# Revit family: FU_Table_Sandler_592-XT
name_source: partatom
category: Furniture
units: mm (PartAtom-declared; Revit-internal decimal feet)

## family parameters
Always vertical = Yes
Cut with Voids When Loaded = No
OmniClass Number = 23.40.20.00
OmniClass Title = General Furniture and Specialties
Room Calculation Point = No
Shared = No
Work Plane-Based = No

## types (5) — shared parameters
Depth = 605 mm  [stored 1.98491 ft]
Description = Table base in stainless steel.
Height = 720 mm  [stored 2.3622 ft]
Manufacturer = Sandler
Model = 592 XT
Top Elevation = 720 mm  [stored 2.3622 ft]
URL = https://www.sandlerseating.com
Width = 605 mm  [stored 1.98491 ft]
zero-valued in all types: Default Elevation

## per-type parameters (varying)
| type | Top Size |
| 592 XT - 40" Square Top (100cm) | FU_TableTops_MT Sqr : 40" Square (100cm) |
| 592 XT - 44" Square Top (110cm) | FU_TableTops_MT Sqr : 44" Square (110cm) |
| 592 XT - 44" Round Top (110cm) | FU_TableTops_MT Rnd : 44" Round (110cm) |
| 592 XT - 51" Round Top (130cm) | FU_TableTops_MT Rnd : 51" Round (130cm) |
| 592 XT - 48" Round Top (120cm) | FU_TableTops_MT Rnd : 47" Round (120cm) |

note: [stored X ft] marks values corroborated as IEEE doubles in the binary element streams (Revit-internal decimal feet)

## geometry (parser evidence)
native form markers: Sweep x7
no freeform markers — native parametric forms only
